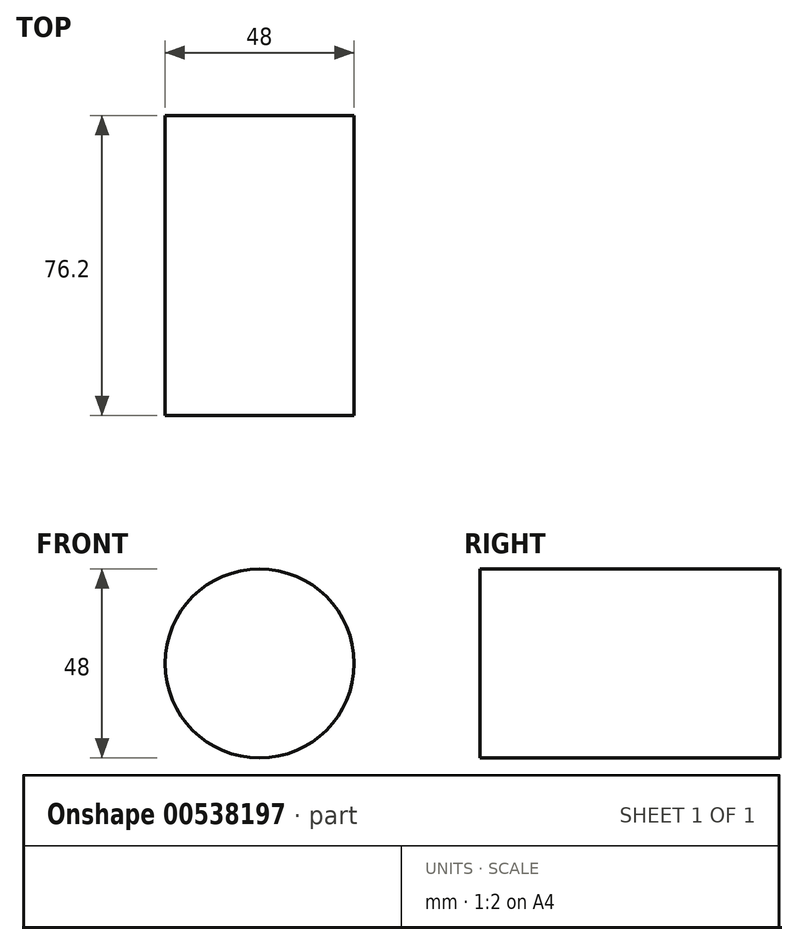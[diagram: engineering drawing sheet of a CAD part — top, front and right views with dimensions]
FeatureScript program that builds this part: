
annotation { "Feature Type Name" : "Feature", "Feature Type Description" : "" }
export const myFeature = defineFeature(function(context is Context, id is Id, definition is map)
    precondition{}
    {
        {
            var Q0;
            Q0=qCreatedBy(makeId("Front.planeOp"),FACE);
            var sketch = newSketch(context, id + "F0", { "sketchPlane" : qUnion([Q0])});
            skCircle(sketch, "E0", {"center": v(0, 0) * mm, "radius": 24 * mm});
            skSolve(sketch);
        }
        {
            var Q0;
            Q0=makeQuery(id+"F0.imprint","IMPRINT",FACE,{"disambiguationData":[TD([[makeQuery(id+"F0.imprint","IMPRINT",EDGE,{"derivedFrom":sQuery(id+"F0.wireOp",EDGE,"E0")}),1.0]])]});
            extrude(context, id + "F1", {"entities" : qUnion([Q0]), "oppositeDirection" : true, "depth" : 76.2 * mm, "offsetDistance" : 25.4 * mm});
        }
    });
